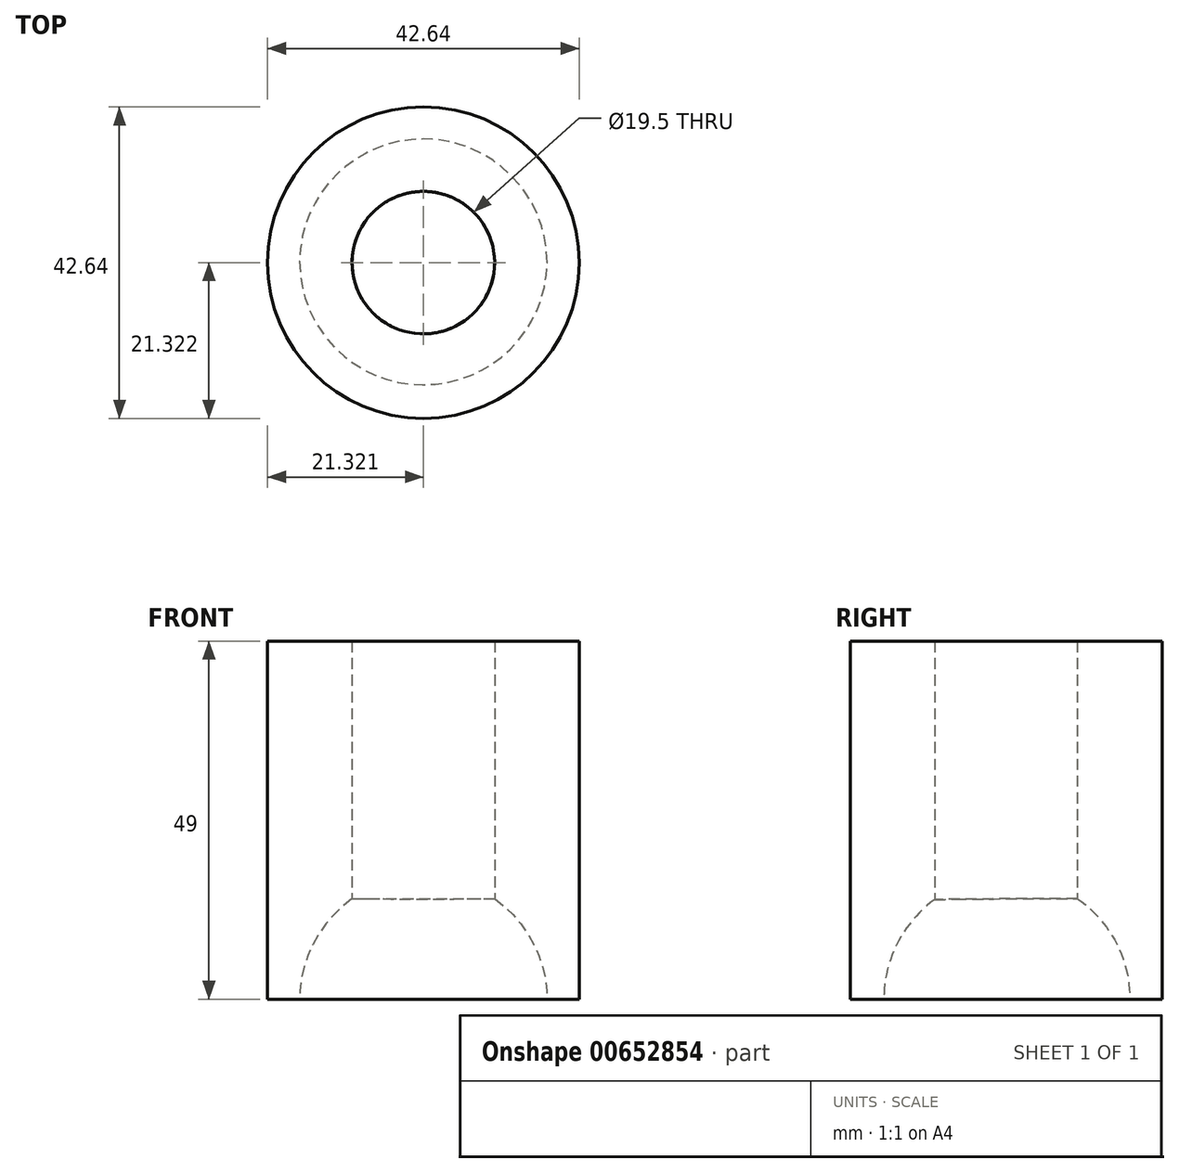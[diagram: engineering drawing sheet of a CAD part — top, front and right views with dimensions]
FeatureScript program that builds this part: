
annotation { "Feature Type Name" : "Feature", "Feature Type Description" : "" }
export const myFeature = defineFeature(function(context is Context, id is Id, definition is map)
    precondition{}
    {
        {
            var Q0;
            Q0=qCreatedBy(makeId("Top.planeOp"),FACE);
            var sketch = newSketch(context, id + "F0", { "sketchPlane" : qUnion([Q0])});
            skCircle(sketch, "E0", {"center": v(-9.46, -22.13) * mm, "radius": 21.32 * mm});
            skArc(sketch, "E1", {"start": v(6.47, -22.12) * mm, "mid": v(-9.37, -6.2) * mm, "end": v(-25.38, -21.94) * mm});
            skLineSegment(sketch, "E2", {"start": v(-25.38, -21.94) * mm, "end": v(6.47, -22.12) * mm});
            skCircle(sketch, "E3", {"center": v(-9.46, -22.13) * mm, "radius": 9.75 * mm});
            skSolve(sketch);
        }
        {
            var Q0;
            Q0=makeQuery(id+"F0.imprint","IMPRINT",FACE,{"disambiguationData":[TD([[makeQuery(id+"F0.imprint","IMPRINT",EDGE,{"derivedFrom":sQuery(id+"F0.wireOp",EDGE,"E1")}),1.0]])]});
            var Q1;
            Q1=makeQuery(id+"F0.imprint","IMPRINT",FACE,{"disambiguationData":[TD([[makeQuery(id+"F0.imprint","IMPRINT",EDGE,{"derivedFrom":sQuery(id+"F0.wireOp",EDGE,"E0")}),1.0]])]});
            extrude(context, id + "F1", {"entities" : qUnion([Q0, Q1]), "depth" : 49 * mm, "offsetDistance" : 25 * mm});
        }
        {
            var Q0;
            {var subQ0=sQuery(id+"F0.wireOp",EDGE,"E1");Q0=makeQuery(id+"F0.imprint","IMPRINT",FACE,{"disambiguationData":[TD([[makeQuery(id+"F0.imprint","IMPRINT",EDGE,{"derivedFrom":subQ0}),1.0]])]});}
            var Q1;
            {var subQ0=sQuery(id+"F0.wireOp",EDGE,"E3");var subQ1=sQuery(id+"F0.wireOp",EDGE,"E2");var subQ2=makeQuery(id+"F0.imprint","INTERSECT",VERTEX,{"disambiguationData":[OD(0.0)],"derivedFrom":[subQ1,subQ0]});Q1=makeQuery(id+"F0.imprint","IMPRINT",FACE,{"disambiguationData":[TD([[makeQuery(id+"F0.imprint","IMPRINT",EDGE,{"disambiguationData":[TD([[subQ2,-1.0]])],"derivedFrom":subQ1}),1.0]])]});}
            var Q2;
            Q2=sQuery(id+"F0.wireOp",EDGE,"E1");
            var Q3;
            Q3=sQuery(id+"F0.wireOp",EDGE,"E2");
            revolve(context, id + "F2", {"entities" : qUnion([Q0, Q1]), "surfaceEntities" : qUnion([Q2]), "axis" : qUnion([Q3]), "revolveType" : RevolveType.FULL});
        }
        {
            var Q0;
            Q0=makeQuery(id+"F2.opRevolve","SWEPT_BODY",BODY,{"disambiguationData":[OSD([sQuery(id+"F0.wireOp",EDGE,"E1"),sQuery(id+"F0.wireOp",EDGE,"E2"),sQuery(id+"F0.wireOp",EDGE,"E3")])]});
            var Q1;
            Q1=makeQuery(id+"F1.opExtrude","SWEPT_BODY",BODY,{"disambiguationData":[OSD([sQuery(id+"F0.wireOp",EDGE,"E0"),sQuery(id+"F0.wireOp",EDGE,"E3")])]});
            var Q2;
            Q2=makeQuery(id+"F2.opRevolve","SWEPT_FACE",FACE,{"disambiguationData":[OSD([sQuery(id+"F0.wireOp",EDGE,"E1")])]});
            booleanBodies(context, id + "F3", {"operationType" : BooleanOperationType.SUBTRACTION, "tools" : qUnion([Q0]), "targets" : qUnion([Q1]), "offset" : true, "entitiesToOffset" : qUnion([Q2]), "offsetDistance" : 1 * mm});
        }
    });
